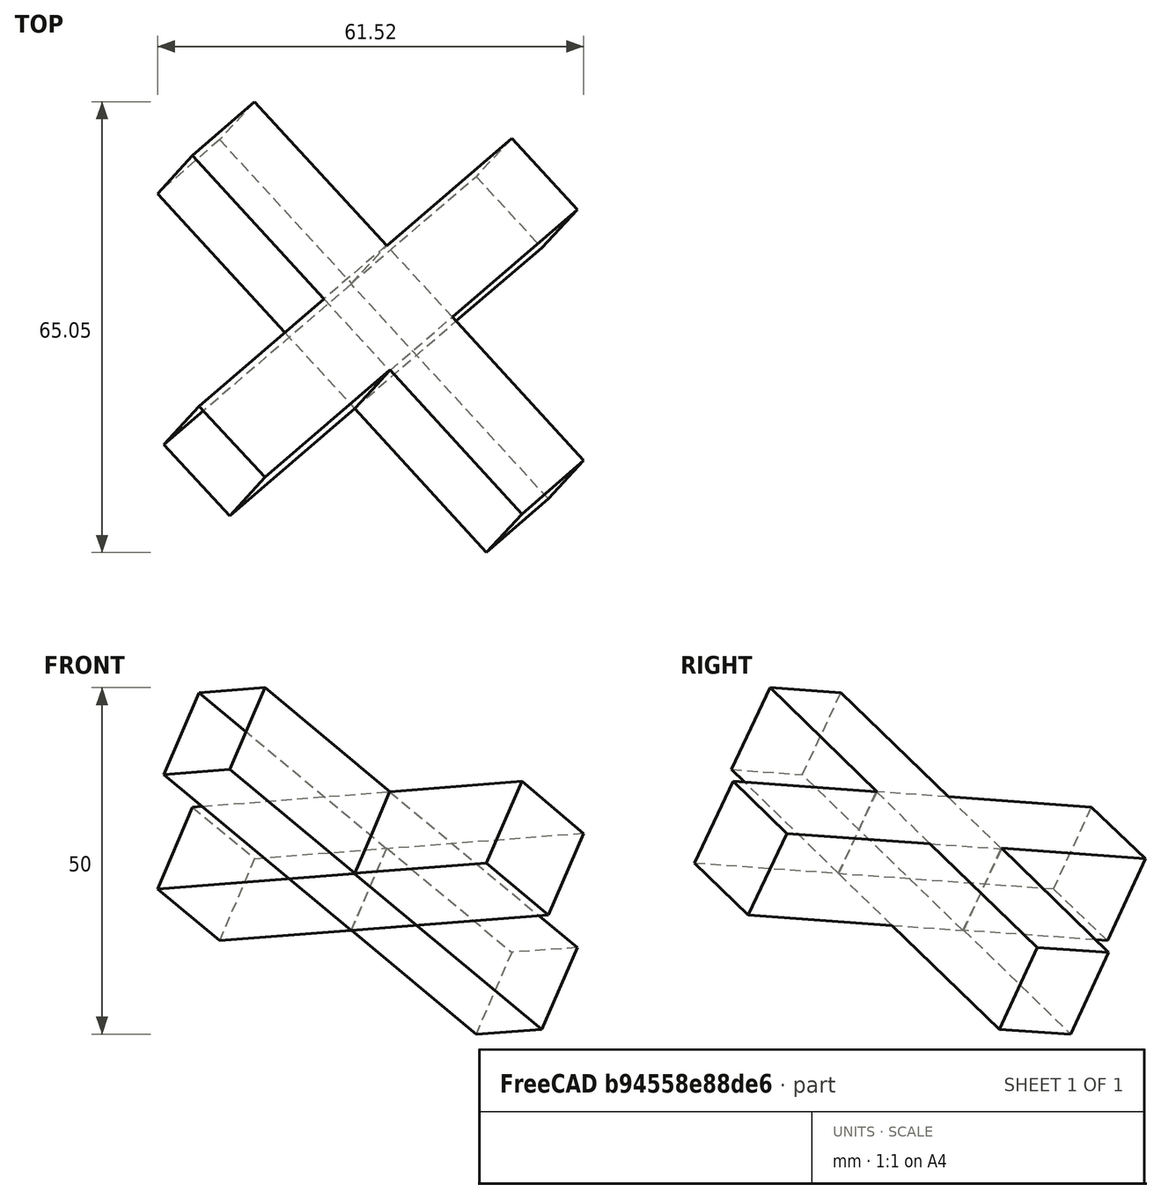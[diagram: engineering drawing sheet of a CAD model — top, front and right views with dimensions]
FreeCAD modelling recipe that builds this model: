
FCSTD DOCUMENT  (FreeCAD 0.15R4671 (Git))
Label: X Time
License: All rights reserved
LicenseURL: http://en.wikipedia.org/wiki/All_rights_reserved
objects: Sketcher::SketchObject×3, Part::Sweep×1
note: 4 computed .brp shape members not serialized (recipe doc carries the construction recipe); baked Part::Feature solids carry a one-line shape summary decoded from their .brp

FEATURE [Sketcher::SketchObject] Sketch
  sketch-geometry (5):
    g0: LineSegment StartX=6.96577 StartY=-7.03406 StartZ=0 EndX=7.03406 EndY=6.96577 EndZ=0
    g1: LineSegment StartX=7.03406 StartY=6.96577 StartZ=0 EndX=-6.96577 EndY=7.03406 EndZ=0
    g2: LineSegment StartX=-6.96577 StartY=7.03406 StartZ=0 EndX=-7.03406 EndY=-6.96577 EndZ=0
    g3: LineSegment StartX=-7.03406 StartY=-6.96577 StartZ=0 EndX=6.96577 EndY=-7.03406 EndZ=0
    g4: Circle [constr] CenterX=0 CenterY=0 CenterZ=0 NormalX=0 NormalY=0 NormalZ=1 Radius=9.89949
  constraints (15):
    c: Coincident(g0,g1)
    c: Coincident(g1,g2)
    c: Coincident(g2,g3)
    c: Coincident(g3,g0)
    c: Equal(g0,g1)
    c: Equal(g0,g2)
    c: Equal(g0,g3)
    c: PointOnObject(g0,g4)
    c: PointOnObject(g1,g4)
    c: PointOnObject(g2,g4)
    c: PointOnObject(g3,g4)
    c: Coincident(g1,g-1)
    c: Coincident(g4,g-1)
    c: Distance(g0) = 14
    c: DistanceY(g2) = -6.96577
FEATURE [Sketcher::SketchObject] Sketch001
FEATURE [Sketcher::SketchObject] Sketch002
  Placement = pos=(0,0,0) rot=(0.57735,0.57735,0.57735;2.0944rad)
  sketch-geometry (5):
    g0: LineSegment StartX=6.96826 StartY=-7.0316 StartZ=0 EndX=7.0316 EndY=6.96826 EndZ=0
    g1: LineSegment StartX=7.0316 StartY=6.96826 StartZ=0 EndX=-6.96826 EndY=7.0316 EndZ=0
    g2: LineSegment StartX=-6.96826 StartY=7.0316 StartZ=0 EndX=-7.0316 EndY=-6.96826 EndZ=0
    g3: LineSegment StartX=-7.0316 StartY=-6.96826 StartZ=0 EndX=6.96826 EndY=-7.0316 EndZ=0
    g4: Circle [constr] CenterX=0 CenterY=0 CenterZ=0 NormalX=0 NormalY=0 NormalZ=1 Radius=9.89949
  constraints (15):
    c: Coincident(g0,g1)
    c: Coincident(g1,g2)
    c: Coincident(g2,g3)
    c: Coincident(g3,g0)
    c: Equal(g0,g1)
    c: Equal(g0,g2)
    c: Equal(g0,g3)
    c: PointOnObject(g0,g4)
    c: PointOnObject(g1,g4)
    c: PointOnObject(g2,g4)
    c: PointOnObject(g3,g4)
    c: Coincident(g1,g-1)
    c: Distance(g0) = 14
    c: Coincident(g4,g-1)
    c: DistanceY(g0) = -7.0316
FEATURE [Part::Sweep] Sweep
  Frenet = false
  Placement = pos=(-4.24099,0.743059,-15.476) rot=(-0.279655,0.565528,0.775868;0.917435rad)
  Sections = -> [Sketch002]
  Solid = true
  Spine = -> Sketch
  Transition = 1
